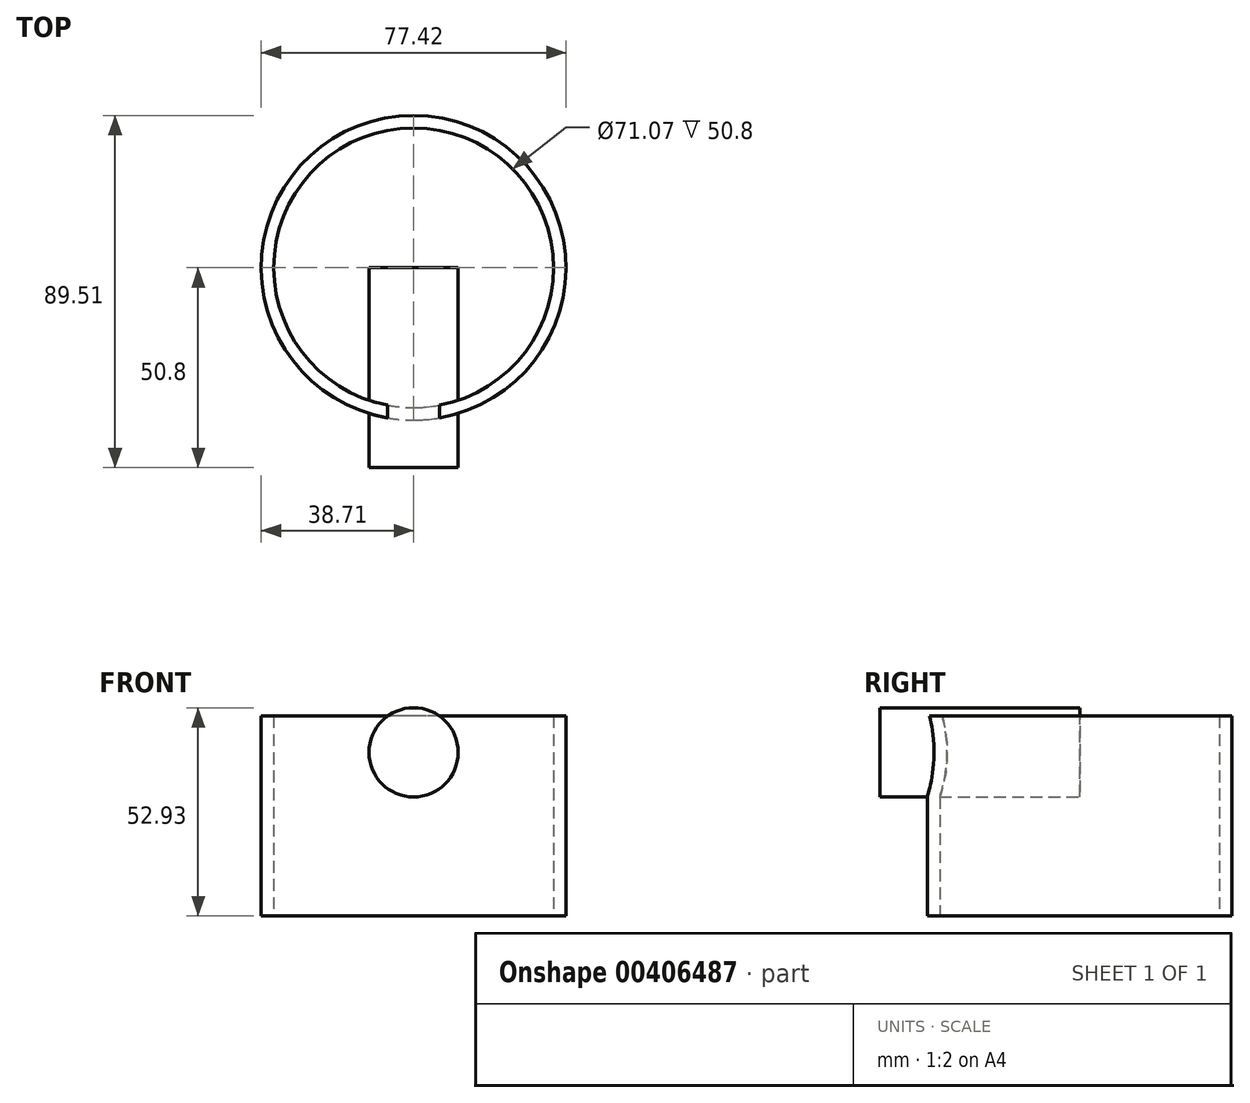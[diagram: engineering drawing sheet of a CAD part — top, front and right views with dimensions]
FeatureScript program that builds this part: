
annotation { "Feature Type Name" : "Feature", "Feature Type Description" : "" }
export const myFeature = defineFeature(function(context is Context, id is Id, definition is map)
    precondition{}
    {
        {
            var Q0;
            Q0=qCreatedBy(makeId("Top.planeOp"),FACE);
            var sketch = newSketch(context, id + "F0", { "sketchPlane" : qUnion([Q0])});
            skCircle(sketch, "E0", {"center": v(0, 0) * mm, "radius": 35.53 * mm});
            skCircle(sketch, "E1.0", {"center": v(0, 0) * mm, "radius": 38.7 * mm});
            skSolve(sketch);
        }
        {
            var Q0;
            Q0 = qSketchRegion(id + "F0", true);
            extrude(context, id + "F1", {"entities" : qUnion([Q0]), "depth" : 50.8 * mm});
        }
        {
            var Q0;
            Q0=qCreatedBy(makeId("Front.planeOp"),FACE);
            var sketch = newSketch(context, id + "F2", { "sketchPlane" : qUnion([Q0])});
            skCircle(sketch, "E2", {"center": v(0, 41.6) * mm, "radius": 11.33 * mm});
            skSolve(sketch);
        }
        {
            var Q0;
            Q0 = qSketchRegion(id + "F2", true);
            extrude(context, id + "F3", {"entities" : qUnion([Q0]), "operationType" : NewBodyOperationType.ADD, "depth" : 50.8 * mm});
        }
    });
